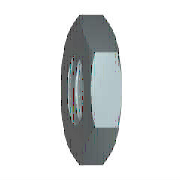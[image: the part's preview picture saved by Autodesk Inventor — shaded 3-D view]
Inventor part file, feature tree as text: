
AUTODESK INVENTOR PART (.ipt)
format: ipt  version: 2015 (Build 190159000, 159)  size: 171,520 bytes
history: native  units: mm (DEFAULTED — no unit token found)
features: sketch x3, chamfer x1, hole x1, other x1, plane x1
ambient origin geometry x7: Origin, YZ Plane, XZ Plane, X Axis, Y Axis, Z Axis, Center Point
bodies: Solid1 (feature_tree), Body (feature_tree)
feature tree (7):
  chamfer  "Chamfer1"  Angle=30.0deg  [1 undecoded]
  hole  "Thread"  [1 undecoded]
  other  "Work Axis1"
  plane  "Work Plane1"
  sketch  "Sketch1"  dims[d0=10.998523mm]
  sketch  "Sketch2"  dims[d1=3.302mm]
  sketch  "Sketch3"  dims[d2=0.0mm d3=30.0deg d4=30.0deg d5=9.525mm d6=9.525mm d7=90.0deg d25=3.683mm d26=6.0mm d27=4.0mm d28=2.0mm d29=14.3117mm d30=8.0mm d31=20.594885mm d8=0.57284mm d9=30.0deg d10=0.57284mm d11=30.0deg d13=0.0mm d14=0.0mm d39=0.0mm d40=0.57284mm d41=0.57284mm d42=0.0mm]
note: 2 required parameter values undecoded (feature->parameter linkage not recoverable at this tier; creation-order binding heuristic only, values carry confidence <= 0.55)
